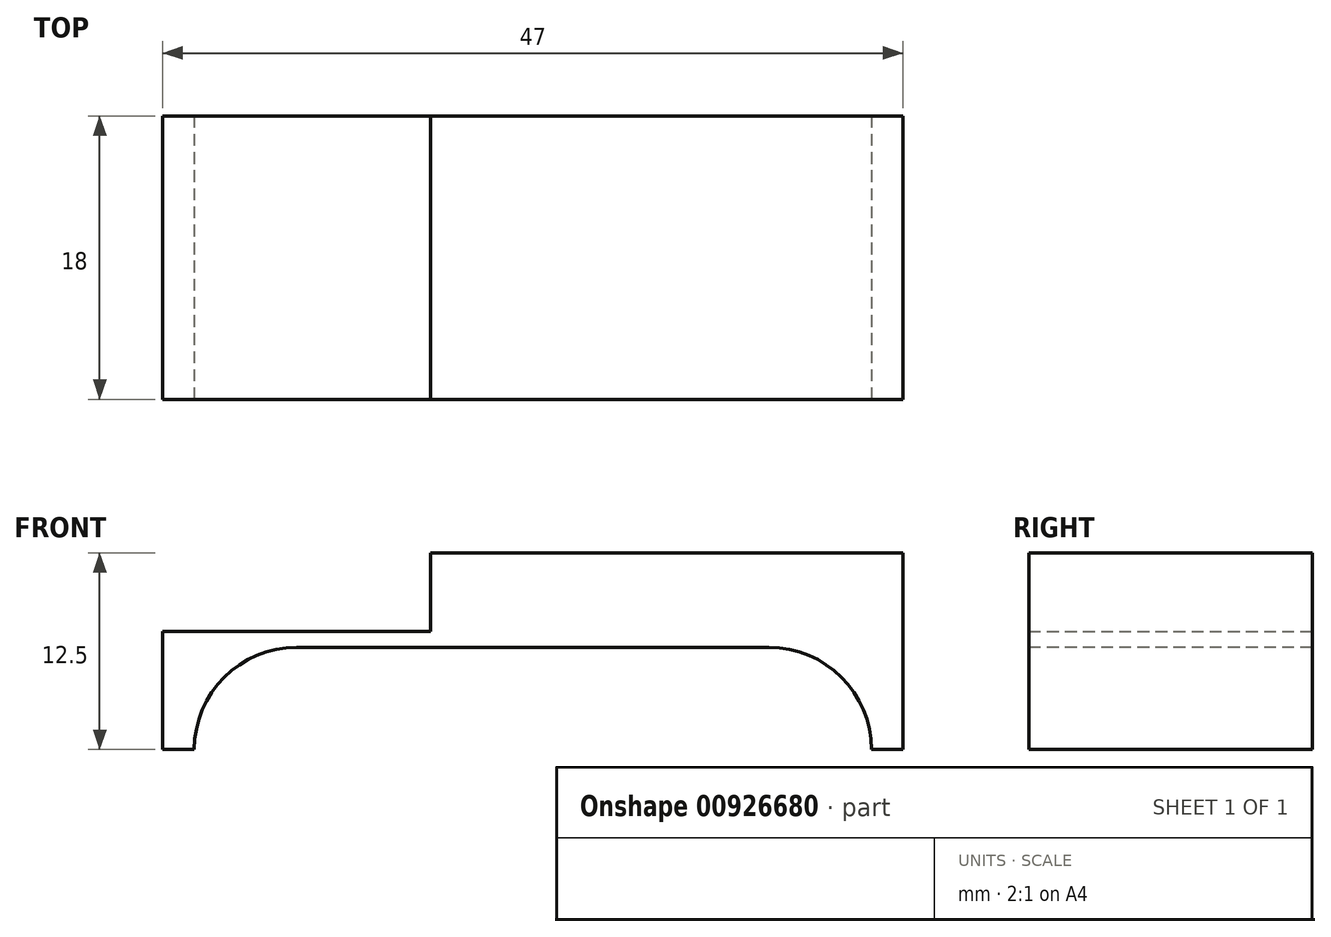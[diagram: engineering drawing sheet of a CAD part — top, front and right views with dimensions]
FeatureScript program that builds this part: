
annotation { "Feature Type Name" : "Feature", "Feature Type Description" : "" }
export const myFeature = defineFeature(function(context is Context, id is Id, definition is map)
    precondition{}
    {
        {
            var Q0;
            Q0=qCreatedBy(makeId("Front.planeOp"),FACE);
            var sketch = newSketch(context, id + "F0", { "sketchPlane" : qUnion([Q0])});
            skLineSegment(sketch, "E0.bottom", {"start": v(0, 0) * mm, "end": v(47, 0) * mm});
            skLineSegment(sketch, "E0.top", {"start": v(0, 7.5) * mm, "end": v(47, 7.5) * mm});
            skLineSegment(sketch, "E0.left", {"start": v(0, 0) * mm, "end": v(0, 7.5) * mm});
            skLineSegment(sketch, "E0.right", {"start": v(47, 0) * mm, "end": v(47, 7.5) * mm});
            skSolve(sketch);
        }
        {
            var Q0;
            Q0 = qSketchRegion(id + "F0", true);
            extrude(context, id + "F1", {"entities" : qUnion([Q0]), "depth" : 18 * mm, "offsetDistance" : 25 * mm});
        }
        {
            var Q0;
            Q0=makeQuery(id+"F1.opExtrude","CAP_FACE",FACE,{"disambiguationData":[OSD([sQuery(id+"F0.wireOp",EDGE,"E0.bottom"),sQuery(id+"F0.wireOp",EDGE,"E0.top"),sQuery(id+"F0.wireOp",EDGE,"E0.left"),sQuery(id+"F0.wireOp",EDGE,"E0.right")])],"isStart":false});
            var sketch = newSketch(context, id + "F2", { "sketchPlane" : qUnion([Q0])});
            skLineSegment(sketch, "E1", {"start": v(0, 0) * mm, "end": v(8.5, 0) * mm});
            skLineSegment(sketch, "E2.bottom", {"start": v(8.5, 0) * mm, "end": v(38.5, 0) * mm});
            skLineSegment(sketch, "E2.top", {"start": v(8.5, 6.5) * mm, "end": v(38.5, 6.5) * mm});
            skLineSegment(sketch, "E2.left", {"start": v(8.5, 0) * mm, "end": v(8.5, 6.5) * mm});
            skLineSegment(sketch, "E2.right", {"start": v(38.5, 0) * mm, "end": v(38.5, 6.5) * mm});
            skSolve(sketch);
        }
        {
            var Q0;
            Q0 = qSketchRegion(id + "F2", true);
            extrude(context, id + "F3", {"entities" : qUnion([Q0]), "operationType" : NewBodyOperationType.REMOVE, "oppositeDirection" : true, "depth" : 25 * mm, "offsetDistance" : 25 * mm});
        }
        {
            var Q0;
            Q0=makeQuery(id+"F1.opExtrude","CAP_FACE",FACE,{"disambiguationData":[OSD([sQuery(id+"F0.wireOp",EDGE,"E0.bottom"),sQuery(id+"F0.wireOp",EDGE,"E0.top"),sQuery(id+"F0.wireOp",EDGE,"E0.left"),sQuery(id+"F0.wireOp",EDGE,"E0.right")])],"isStart":false});
            var sketch = newSketch(context, id + "F4", { "sketchPlane" : qUnion([Q0])});
            skCircle(sketch, "E3", {"center": v(8.5, 0) * mm, "radius": 6.5 * mm});
            skSolve(sketch);
        }
        {
            var Q0;
            Q0 = qSketchRegion(id + "F4", true);
            extrude(context, id + "F5", {"entities" : qUnion([Q0]), "operationType" : NewBodyOperationType.REMOVE, "oppositeDirection" : true, "depth" : 25 * mm, "offsetDistance" : 25 * mm});
        }
        {
            var Q0;
            Q0=makeQuery(id+"F1.opExtrude","CAP_FACE",FACE,{"disambiguationData":[OSD([sQuery(id+"F0.wireOp",EDGE,"E0.bottom"),sQuery(id+"F0.wireOp",EDGE,"E0.top"),sQuery(id+"F0.wireOp",EDGE,"E0.left"),sQuery(id+"F0.wireOp",EDGE,"E0.right")])],"isStart":false});
            var sketch = newSketch(context, id + "F6", { "sketchPlane" : qUnion([Q0])});
            skCircle(sketch, "E4", {"center": v(38.5, 0) * mm, "radius": 6.5 * mm});
            skSolve(sketch);
        }
        {
            var Q0;
            Q0 = qSketchRegion(id + "F6", true);
            extrude(context, id + "F7", {"entities" : qUnion([Q0]), "operationType" : NewBodyOperationType.REMOVE, "oppositeDirection" : true, "depth" : 25 * mm, "offsetDistance" : 25 * mm});
        }
        {
            var Q0;
            Q0=makeQuery(id+"F1.opExtrude","SWEPT_FACE",FACE,{"disambiguationData":[OSD([sQuery(id+"F0.wireOp",EDGE,"E0.top")])]});
            var sketch = newSketch(context, id + "F8", { "sketchPlane" : qUnion([Q0])});
            skLineSegment(sketch, "E5.bottom", {"start": v(0, -18) * mm, "end": v(17, -18) * mm});
            skLineSegment(sketch, "E5.top", {"start": v(0, 0) * mm, "end": v(17, 0) * mm});
            skLineSegment(sketch, "E5.left", {"start": v(0, -18) * mm, "end": v(0, 0) * mm});
            skLineSegment(sketch, "E5.right", {"start": v(17, -18) * mm, "end": v(17, 0) * mm});
            skSolve(sketch);
        }
        {
            var Q0;
            {var subQ0=sQuery(id+"F8.wireOp",EDGE,"E5.right");Q0=makeQuery(id+"F8.imprint","IMPRINT",FACE,{"disambiguationData":[TD([[makeQuery(id+"F8.imprint","IMPRINT",EDGE,{"derivedFrom":subQ0}),-1.0]])]});}
            extrude(context, id + "F9", {"entities" : qUnion([Q0]), "operationType" : NewBodyOperationType.ADD, "depth" : 5 * mm, "offsetDistance" : 25 * mm});
        }
    });
